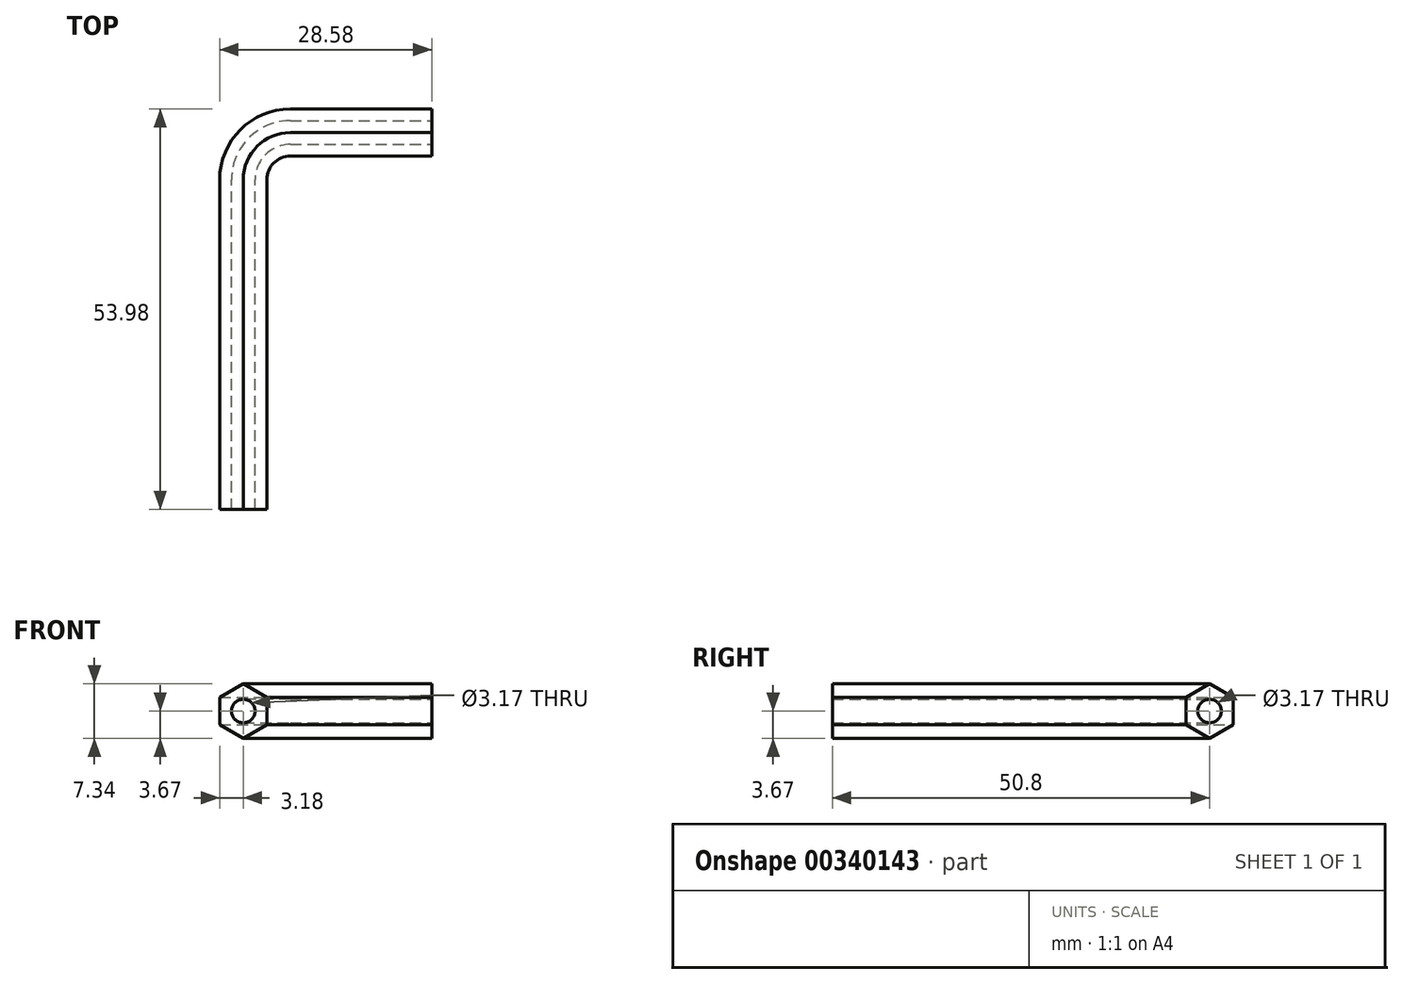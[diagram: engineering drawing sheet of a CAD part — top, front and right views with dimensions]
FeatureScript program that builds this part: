
annotation { "Feature Type Name" : "Feature", "Feature Type Description" : "" }
export const myFeature = defineFeature(function(context is Context, id is Id, definition is map)
    precondition{}
    {
        {
            var Q0;
            Q0=qCreatedBy(makeId("Front.planeOp"),FACE);
            var sketch = newSketch(context, id + "F0", { "sketchPlane" : qUnion([Q0])});
            skCircle(sketch, "E0.cCircle", {"center": v(0, 0) * mm, "radius": 3.17 * mm, "construction": true});
            skLineSegment(sketch, "E0.0", {"start": v(3.17, 1.83) * mm, "end": v(3.17, -1.83) * mm});
            skLineSegment(sketch, "E0.1", {"start": v(3.17, -1.83) * mm, "end": v(0, -3.67) * mm});
            skLineSegment(sketch, "E0.2", {"start": v(0, -3.67) * mm, "end": v(-3.17, -1.83) * mm});
            skLineSegment(sketch, "E0.3", {"start": v(-3.17, -1.83) * mm, "end": v(-3.18, 1.83) * mm});
            skLineSegment(sketch, "E0.4", {"start": v(-3.18, 1.83) * mm, "end": v(0, 3.67) * mm});
            skLineSegment(sketch, "E0.5", {"start": v(0, 3.67) * mm, "end": v(3.17, 1.83) * mm});
            skPoint(sketch, "E0.0.midPoint", {"position": v(3.17, 0) * mm});
            skSolve(sketch);
        }
        {
            var Q0;
            Q0=qCreatedBy(makeId("Top.planeOp"),FACE);
            var sketch = newSketch(context, id + "F1", { "sketchPlane" : qUnion([Q0])});
            skLineSegment(sketch, "E1", {"start": v(0, 0) * mm, "end": v(0, 44.45) * mm});
            skLineSegment(sketch, "E2", {"start": v(6.35, 50.8) * mm, "end": v(25.4, 50.8) * mm});
            skPoint(sketch, "E3.visualSharp", {"position": v(0, 50.8) * mm});
            skArc(sketch, "E3.filletArc", {"start": v(6.35, 50.8) * mm, "mid": v(1.86, 48.94) * mm, "end": v(0, 44.45) * mm});
            skSolve(sketch);
        }
        {
            var Q0;
            Q0=makeQuery(id+"F0.imprint","IMPRINT",FACE,{"disambiguationData":[TD([[makeQuery(id+"F0.imprint","IMPRINT",EDGE,{"derivedFrom":sQuery(id+"F0.wireOp",EDGE,"E0.0")}),-1.0]])]});
            var Q1;
            Q1=sQuery(id+"F1.wireOp",EDGE,"E1");
            var Q2;
            Q2=sQuery(id+"F1.wireOp",EDGE,"E3.filletArc");
            var Q3;
            Q3=sQuery(id+"F1.wireOp",EDGE,"E2");
            sweep(context, id + "F2", {"profiles" : qUnion([Q0]), "path" : qUnion([Q1, Q2, Q3])});
        }
        {
            var Q0;
            Q0=makeQuery(id+"F2.opSweep","CAP_FACE",FACE,{"disambiguationData":[OSD([sQuery(id+"F0.wireOp",EDGE,"E0.0"),sQuery(id+"F0.wireOp",EDGE,"E0.1"),sQuery(id+"F0.wireOp",EDGE,"E0.2"),sQuery(id+"F0.wireOp",EDGE,"E0.3"),sQuery(id+"F0.wireOp",EDGE,"E0.4"),sQuery(id+"F0.wireOp",EDGE,"E0.5"),sQuery(id+"F1.wireOp",VERTEX,"E1.start")])],"isStart":true});
            var sketch = newSketch(context, id + "F3", { "sketchPlane" : qUnion([Q0])});
            skCircle(sketch, "E4", {"center": v(0, 0) * mm, "radius": 1.59 * mm});
            skSolve(sketch);
        }
        {
            var Q0;
            Q0=makeQuery(id+"F3.imprint","IMPRINT",FACE,{"disambiguationData":[TD([[makeQuery(id+"F3.imprint","IMPRINT",EDGE,{"derivedFrom":sQuery(id+"F3.wireOp",EDGE,"E4")}),1.0]])]});
            var Q1;
            Q1=makeQuery(id+"F2.opSweep","SWEPT_EDGE",EDGE,{"disambiguationData":[OSD([sQuery(id+"F0.wireOp",EDGE,"E0.0"),sQuery(id+"F0.wireOp",EDGE,"E0.1"),sQuery(id+"F1.wireOp",EDGE,"E1")])]});
            var Q2;
            Q2=makeQuery(id+"F2.opSweep","SWEPT_EDGE",EDGE,{"disambiguationData":[OSD([sQuery(id+"F0.wireOp",EDGE,"E0.0"),sQuery(id+"F0.wireOp",EDGE,"E0.1"),sQuery(id+"F1.wireOp",EDGE,"E3.filletArc")])]});
            var Q3;
            Q3=makeQuery(id+"F2.opSweep","SWEPT_EDGE",EDGE,{"disambiguationData":[OSD([sQuery(id+"F0.wireOp",EDGE,"E0.0"),sQuery(id+"F0.wireOp",EDGE,"E0.1"),sQuery(id+"F1.wireOp",EDGE,"E2")])]});
            sweep(context, id + "F4", {"operationType" : NewBodyOperationType.REMOVE, "profiles" : qUnion([Q0]), "path" : qUnion([Q1, Q2, Q3])});
        }
    });
